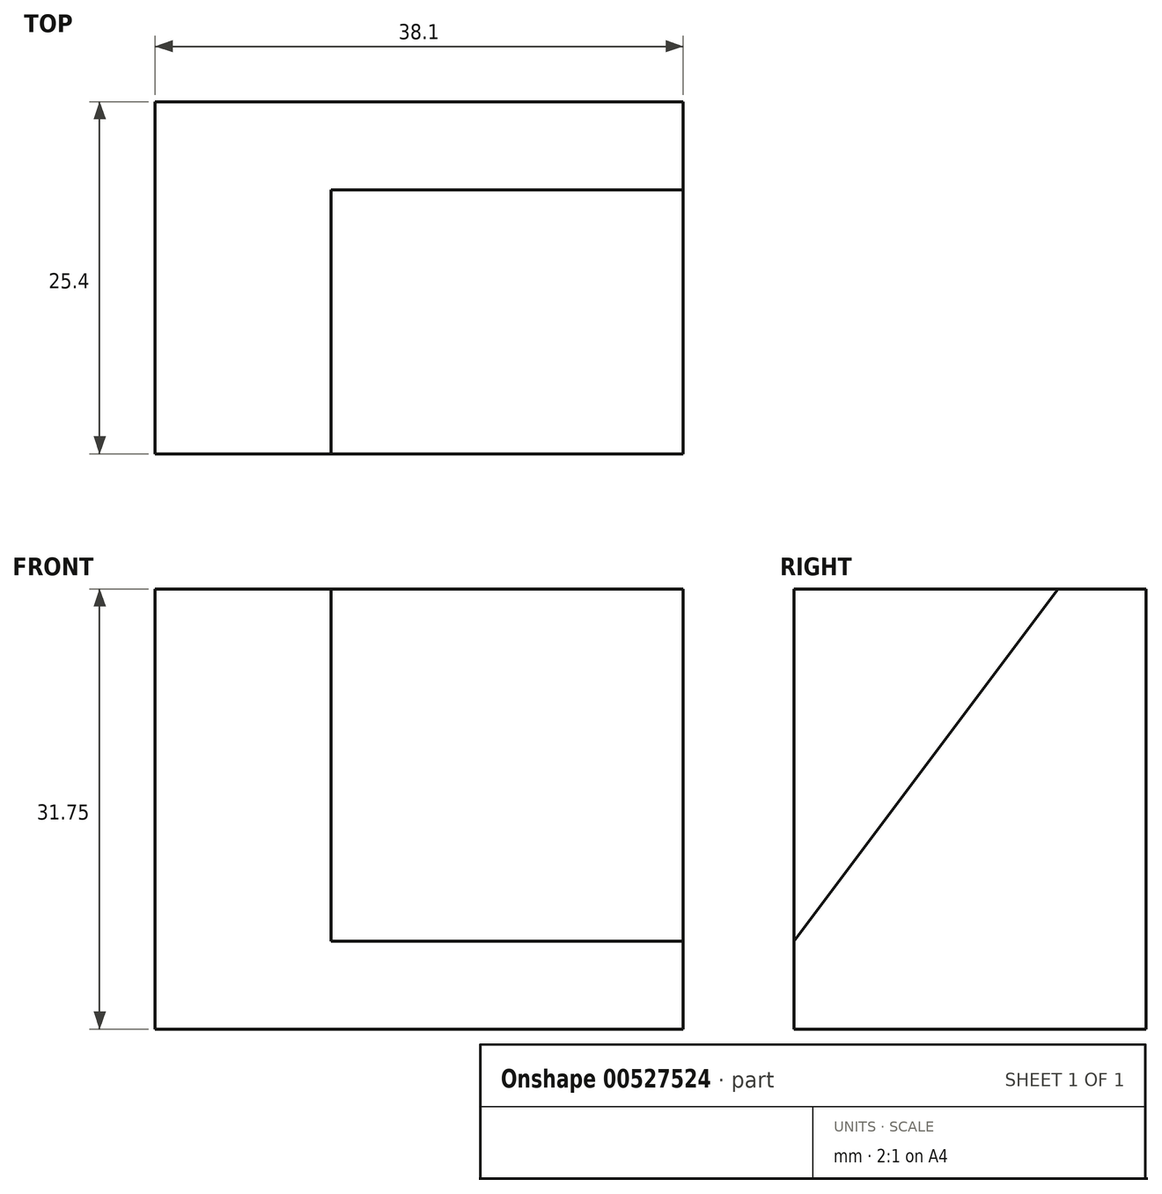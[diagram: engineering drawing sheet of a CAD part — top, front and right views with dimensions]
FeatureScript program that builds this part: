
annotation { "Feature Type Name" : "Feature", "Feature Type Description" : "" }
export const myFeature = defineFeature(function(context is Context, id is Id, definition is map)
    precondition{}
    {
        {
            var Q0;
            Q0=qCreatedBy(makeId("Right.planeOp"),FACE);
            var sketch = newSketch(context, id + "F0", { "sketchPlane" : qUnion([Q0])});
            skLineSegment(sketch, "E0", {"start": v(0, 0) * mm, "end": v(0, 6.35) * mm});
            skLineSegment(sketch, "E1", {"start": v(0, 6.35) * mm, "end": v(19.05, 31.75) * mm});
            skLineSegment(sketch, "E2", {"start": v(19.05, 31.75) * mm, "end": v(25.4, 31.75) * mm});
            skLineSegment(sketch, "E3", {"start": v(25.4, 31.75) * mm, "end": v(25.4, 0) * mm});
            skLineSegment(sketch, "E4", {"start": v(25.4, 0) * mm, "end": v(0, 0) * mm});
            skSolve(sketch);
        }
        {
            var Q0;
            Q0=makeQuery(id+"F0.imprint","IMPRINT",FACE,{"disambiguationData":[TD([[makeQuery(id+"F0.imprint","IMPRINT",EDGE,{"derivedFrom":sQuery(id+"F0.wireOp",EDGE,"E0")}),-1.0]])]});
            extrude(context, id + "F1", {"entities" : qUnion([Q0]), "depth" : 25.4 * mm, "offsetDistance" : 25.4 * mm});
        }
        {
            var Q0;
            Q0=makeQuery(id+"F1.opExtrude","CAP_FACE",FACE,{"disambiguationData":[OSD([sQuery(id+"F0.wireOp",EDGE,"E0"),sQuery(id+"F0.wireOp",EDGE,"E1"),sQuery(id+"F0.wireOp",EDGE,"E2"),sQuery(id+"F0.wireOp",EDGE,"E3"),sQuery(id+"F0.wireOp",EDGE,"E4")])],"isStart":true});
            var sketch = newSketch(context, id + "F2", { "sketchPlane" : qUnion([Q0])});
            skLineSegment(sketch, "E5", {"start": v(-25.4, 31.75) * mm, "end": v(0, 31.75) * mm});
            skLineSegment(sketch, "E6", {"start": v(0, 31.75) * mm, "end": v(0, 0) * mm});
            skLineSegment(sketch, "E7", {"start": v(0, 0) * mm, "end": v(-25.4, 0) * mm});
            skLineSegment(sketch, "E8", {"start": v(-25.4, 0) * mm, "end": v(-25.4, 31.75) * mm});
            skSolve(sketch);
        }
        {
            var Q0;
            {var subQ1=sQuery(id+"F2.wireOp",EDGE,"E7");Q0=makeQuery(id+"F2.imprint","IMPRINT",FACE,{"disambiguationData":[TD([[makeQuery(id+"F2.imprint","IMPRINT",EDGE,{"derivedFrom":subQ1}),1.0]])]});}
            var Q1;
            {var subQ1=makeQuery(id+"F1.opExtrude","CAP_EDGE",EDGE,{"disambiguationData":[OSD([sQuery(id+"F0.wireOp",EDGE,"E1")])],"isStart":true});Q1=makeQuery(id+"F2.imprint","IMPRINT",FACE,{"disambiguationData":[TD([[makeQuery(id+"F2.imprint","IMPRINT",EDGE,{"derivedFrom":subQ1}),-1.0]])]});}
            extrude(context, id + "F3", {"entities" : qUnion([Q0, Q1]), "operationType" : NewBodyOperationType.ADD, "depth" : 12.7 * mm, "offsetDistance" : 25.4 * mm});
        }
    });
